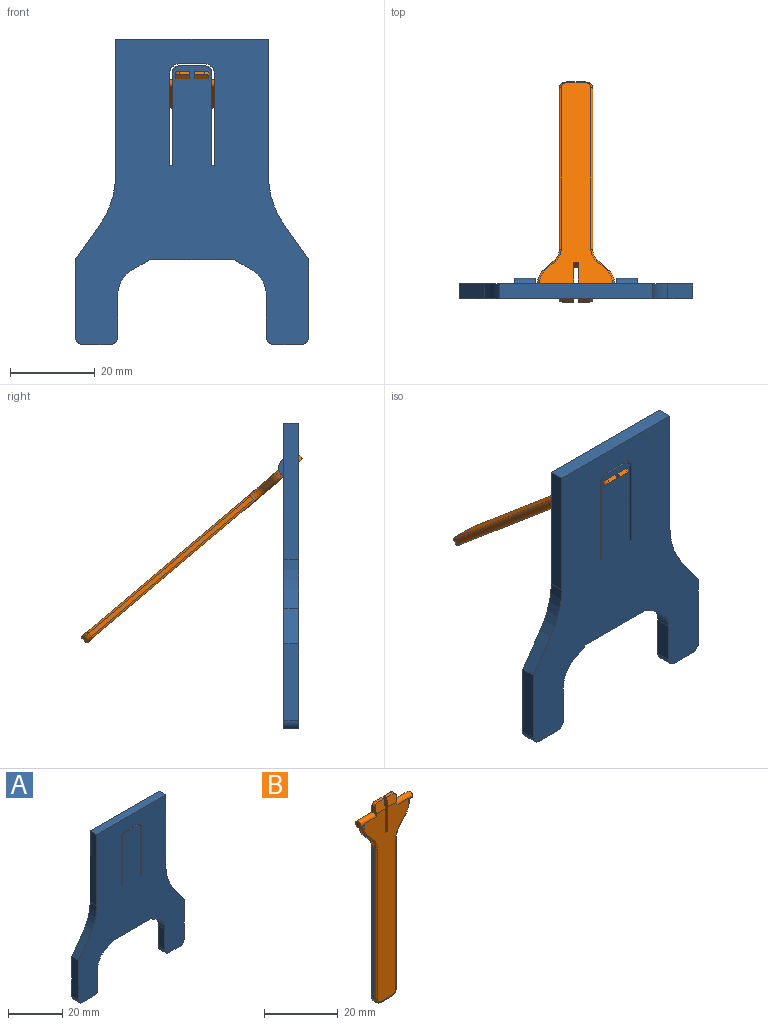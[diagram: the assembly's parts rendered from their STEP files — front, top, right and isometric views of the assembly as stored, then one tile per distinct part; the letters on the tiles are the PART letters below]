
ASSEMBLY  parts=2 mates=1
PART A: 114 faces, bbox 55x4.8x72 mm
  f0: plane 21.71x1.7mm, normal (1,0,0), area 20.6mm2, adj f4,f6,f42,f102,f103,f106,f107,f108
  f1: plane 6x1.6mm, normal (0,0,1), area 9.6mm2, adj f3,f42,f103,f104
  f2: plane 21.71x1.7mm, normal (-1,0,0), area 20.6mm2, adj f4,f6,f42,f104,f105,f106,f107,f108
  f3: cylinder r=0.5mm len=8.88mm, axis (1,0,0), area 7.4mm2, adj f1,f5,f103,f104
  f4: cylinder r=0.5mm len=9.4mm, axis (1,0,0), area 8.7mm2, adj f0,f2,f5,f103,f104,f113
  f5: cylinder r=0.26mm len=9.26mm, axis (1,0,0), area 4.4mm2, adj f3,f4,f103,f104
  f6: plane 39.63x10.4mm, normal (0,1,0), area 394.8mm2, adj f0,f2,f23,f43,f48,f102,f105,f106
  f7: cylinder r=2.2mm len=3.5mm, axis (0,1,0), area 12.1mm2, adj f10,f42,f43,f46
  f8: plane 13.2x5mm, normal (0,1,0), area 42mm2, adj f12,f13,f14,f15,f48,f49,f50,f97
  f9: plane 72x55mm, normal (0,1,0), area 665.1mm2, adj f15,f16,f20,f21,f22,f23,f24,f25
  f10: plane 29x5mm, normal (0,1,0), area 59.9mm2, adj f7,f12,f19,f43,f46,f47,f48,f51
  f11: plane 13.2x5mm, normal (0,1,0), area 42mm2, adj f16,f17,f18,f19,f43,f44,f45,f92
  f12: plane 5x2.7mm, normal (0,0,-1), area 11.8mm2, adj f8,f10,f14,f48,f97,f99
  f13: plane 0.67x0.53mm, normal (-1,0,0), area 0.2mm2, adj f8,f15,f98
  f14: plane 0.23x0.23mm, normal (-1,0,0), area 0mm2, adj f8,f12,f99
  f15: cylinder r=6.2mm len=4.06mm, axis (0,1,0), area 11.6mm2, adj f8,f9,f13,f49,f98
  f16: cylinder r=6.2mm len=4.06mm, axis (0,1,0), area 11.6mm2, adj f9,f11,f17,f45,f93
  f17: plane 0.67x0.53mm, normal (1,0,0), area 0.2mm2, adj f11,f16,f93
  f18: plane 0.23x0.23mm, normal (1,0,0), area 0mm2, adj f11,f19,f94
  f19: plane 5x2.7mm, normal (0,0,-1), area 11.8mm2, adj f10,f11,f18,f43,f92,f94
  f20: plane 9.63x3.5mm, normal (1,0,0), area 33.7mm2, adj f9,f21,f41,f42
  f21: cylinder r=7mm len=6.06mm, axis (0,1,0), area 25.7mm2, adj f9,f20,f22,f42
  f22: plane 4x3.5mm, normal (0.5,0,-0.87), area 16.2mm2, adj f9,f21,f23,f42
  f23: plane 20x3.5mm, normal (0,0,-1), area 41.9mm2, adj f6,f9,f22,f24,f42,f43,f48
  f24: plane 4x3.5mm, normal (-0.5,0,-0.87), area 16.2mm2, adj f9,f23,f25,f42
  f25: cylinder r=7mm len=6.06mm, axis (0,1,0), area 25.7mm2, adj f9,f24,f26,f42
  f26: plane 9.63x3.5mm, normal (-1,0,0), area 33.7mm2, adj f9,f25,f27,f42
  f27: cylinder r=2mm len=3.5mm, axis (0,1,0), area 11mm2, adj f9,f26,f28,f42
  f28: plane 6x3.5mm, normal (0,0,-1), area 21mm2, adj f9,f27,f29,f42
  f29: cylinder r=2mm len=3.5mm, axis (0,1,0), area 11mm2, adj f9,f28,f30,f42
  f30: plane 18x3.5mm, normal (1,0,0), area 63mm2, adj f9,f29,f31,f42
  f31: plane 8.4x5.88mm, normal (0.82,0,0.57), area 35.9mm2, adj f9,f30,f32,f42
  f32: cylinder r=20mm len=11.47mm, axis (0,1,0), area 42.8mm2, adj f9,f31,f33,f42
  f33: plane 32.13x3.5mm, normal (1,0,0), area 112.4mm2, adj f9,f32,f34,f42
  f34: plane 36x3.5mm, normal (0,0,1), area 126mm2, adj f9,f33,f35,f42
  f35: plane 32.13x3.5mm, normal (-1,0,0), area 112.4mm2, adj f9,f34,f36,f42
  f36: cylinder r=20mm len=11.47mm, axis (0,1,0), area 42.8mm2, adj f9,f35,f37,f42
  f37: plane 8.4x5.88mm, normal (-0.82,0,0.57), area 35.9mm2, adj f9,f36,f38,f42
  f38: plane 18x3.5mm, normal (-1,0,0), area 63mm2, adj f9,f37,f39,f42
  f39: cylinder r=2mm len=3.5mm, axis (0,1,0), area 11mm2, adj f9,f38,f40,f42
  f40: plane 6x3.5mm, normal (0,0,-1), area 21mm2, adj f9,f39,f41,f42
  f41: cylinder r=2mm len=3.5mm, axis (0,1,0), area 11mm2, adj f9,f20,f40,f42
  f42: plane 72x55mm, normal (0,-1,0), area 2415.3mm2, adj f0,f1,f2,f7,f20,f21,f22,f23
  f43: plane 44x3.5mm, normal (1,0,0), area 100.5mm2, adj f6,f7,f9,f10,f11,f19,f23,f42
  f44: cylinder r=3.8mm len=2.7mm, axis (0,1,0), area 7.3mm2, adj f9,f11,f43,f45
  f45: plane 2.95x2.7mm, normal (0.76,0,0.65), area 10.5mm2, adj f9,f11,f16,f44
  f46: plane 6x3.5mm, normal (0,0,-1), area 21mm2, adj f7,f10,f42,f47
  f47: cylinder r=2.2mm len=3.5mm, axis (0,1,0), area 12.1mm2, adj f10,f42,f46,f48
  f48: plane 44x3.5mm, normal (-1,0,0), area 100.5mm2, adj f6,f8,f9,f10,f12,f23,f42,f47
  f49: plane 2.95x2.7mm, normal (-0.76,0,0.65), area 10.5mm2, adj f8,f9,f15,f50
  f50: cylinder r=3.8mm len=2.7mm, axis (0,1,0), area 7.3mm2, adj f8,f9,f48,f49
  f51: plane 7x2.75mm, normal (1,0,0), area 14mm2, adj f9,f10,f54,f55,f78,f98
  f52: plane 7x2.75mm, normal (-1,0,0), area 14mm2, adj f9,f10,f56,f78,f91,f93
  f53: plane 1.5x0.35mm, normal (-1,0,0), area 0.4mm2, adj f10,f58,f78,f91
  f54: cylinder r=3.5mm len=2.43mm, axis (1,0,0), area 3.7mm2, adj f9,f51,f78,f87
  f55: cylinder r=3.5mm len=2.3mm, axis (1,0,0), area 3.5mm2, adj f10,f51,f78,f86
  f56: cylinder r=3.5mm len=2.43mm, axis (1,0,0), area 3.7mm2, adj f9,f52,f78,f82
  f57: cylinder r=4.2mm len=4.03mm, axis (0,1,0), area 8.1mm2, adj f10,f78,f84,f85
  f58: plane 5.18x1.5mm, normal (0,0,1), area 7.8mm2, adj f10,f53,f78,f83
  f59: plane 3.34x1.5mm, normal (0,0,1), area 5mm2, adj f9,f64,f78,f90
  f60: plane 9.63x1.5mm, normal (-1,0,0), area 14.4mm2, adj f9,f61,f77,f78
  f61: cylinder r=9mm len=7.79mm, axis (0,1,0), area 14.1mm2, adj f9,f60,f62,f78
  f62: plane 4.46x2.58mm, normal (-0.5,0,0.87), area 7.7mm2, adj f9,f61,f63,f78
  f63: plane 3.34x1.5mm, normal (0,0,1), area 5mm2, adj f9,f62,f78,f79
  f64: plane 4.46x2.58mm, normal (0.5,0,0.87), area 7.7mm2, adj f9,f59,f65,f78
  f65: cylinder r=9mm len=7.79mm, axis (0,1,0), area 14.1mm2, adj f9,f64,f66,f78
  f66: plane 9.63x1.5mm, normal (1,0,0), area 14.4mm2, adj f9,f65,f67,f78
  f67: plane 6x1.5mm, normal (0,0,1), area 9mm2, adj f9,f66,f68,f78
  f68: plane 17.37x1.5mm, normal (-1,0,0), area 26.1mm2, adj f9,f67,f69,f78
  f69: plane 7.89x5.52mm, normal (-0.82,0,-0.57), area 14.4mm2, adj f9,f68,f70,f78
  f70: cylinder r=22mm len=12.62mm, axis (0,1,0), area 20.2mm2, adj f9,f69,f71,f78
  f71: plane 30.13x1.5mm, normal (-1,0,0), area 45.2mm2, adj f9,f70,f72,f78
  f72: plane 32x1.5mm, normal (0,0,-1), area 48mm2, adj f9,f71,f73,f78
  f73: plane 30.13x1.5mm, normal (1,0,0), area 45.2mm2, adj f9,f72,f74,f78
  f74: cylinder r=22mm len=12.62mm, axis (0,1,0), area 20.2mm2, adj f9,f73,f75,f78
  f75: plane 7.89x5.52mm, normal (0.82,0,-0.57), area 14.4mm2, adj f9,f74,f76,f78
  f76: plane 17.37x1.5mm, normal (1,0,0), area 26.1mm2, adj f9,f75,f77,f78
  f77: plane 6x1.5mm, normal (0,0,1), area 9mm2, adj f9,f60,f76,f78
  f78: plane 68x51mm, normal (0,1,0), area 1115.3mm2, adj f51,f52,f53,f54,f55,f56,f57,f58
  f79: plane 28x1.5mm, normal (-1,0,0), area 42mm2, adj f9,f63,f78,f80
  f80: cylinder r=1.8mm len=1.5mm, axis (0,1,0), area 1.9mm2, adj f9,f78,f79,f81
  f81: plane 2.95x2.56mm, normal (-0.76,0,-0.65), area 5.9mm2, adj f9,f78,f80,f82
  f82: cylinder r=8.2mm len=4.02mm, axis (0,1,0), area 6.6mm2, adj f9,f56,f78,f81
  f83: cylinder r=4.2mm len=4.03mm, axis (0,1,0), area 8.1mm2, adj f10,f58,f78,f84
  f84: plane 6x1.5mm, normal (0,0,1), area 9mm2, adj f10,f57,f78,f83
  f85: plane 5.18x1.5mm, normal (0,0,1), area 7.8mm2, adj f10,f57,f78,f86
  f86: plane 1.5x0.35mm, normal (1,0,0), area 0.4mm2, adj f10,f55,f78,f85
  f87: cylinder r=8.2mm len=4.02mm, axis (0,1,0), area 6.6mm2, adj f9,f54,f78,f88
  f88: plane 2.95x2.56mm, normal (0.76,0,-0.65), area 5.9mm2, adj f9,f78,f87,f89
  f89: cylinder r=1.8mm len=1.5mm, axis (0,1,0), area 1.9mm2, adj f9,f78,f88,f90
  f90: plane 28x1.5mm, normal (1,0,0), area 42mm2, adj f9,f59,f78,f89
  f91: cylinder r=3.5mm len=2.3mm, axis (1,0,0), area 3.5mm2, adj f10,f52,f53,f78
  f92: plane 4.27x3.95mm, normal (1,0,0), area 6.7mm2, adj f10,f11,f19,f93,f94,f95
  f93: cylinder r=2.25mm len=5mm, axis (-1,0,0), area 27.1mm2, adj f9,f10,f11,f16,f17,f52,f92
  f94: cylinder r=2.25mm len=0.7mm, axis (-1,0,0), area 0.2mm2, adj f11,f18,f19,f92
  f95: cylinder r=1.5mm len=3mm, axis (1,0,0), area 28.3mm2, adj f92,f96
  f96: plane 3x3mm, normal (1,0,0), area 7.1mm2, adj f95
  f97: plane 4.27x3.95mm, normal (-1,0,0), area 6.7mm2, adj f8,f10,f12,f98,f99,f100
  f98: cylinder r=2.25mm len=5mm, axis (-1,0,0), area 27.1mm2, adj f8,f9,f10,f13,f15,f51,f97
  f99: cylinder r=2.25mm len=0.7mm, axis (-1,0,0), area 0.2mm2, adj f8,f12,f14,f97
  f100: cylinder r=1.5mm len=3mm, axis (1,0,0), area 28.3mm2, adj f97,f101
  f101: plane 3x3mm, normal (-1,0,0), area 7.1mm2, adj f100
  f102: plane 0.8x0.5mm, normal (0,0,1), area 0.4mm2, adj f0,f6,f42,f48
  f103: cylinder r=1.7mm len=1.7mm, axis (0,1,0), area 4mm2, adj f0,f1,f3,f4,f5,f42
  f104: cylinder r=1.7mm len=1.7mm, axis (0,1,0), area 4mm2, adj f1,f2,f3,f4,f5,f42
  f105: plane 0.8x0.5mm, normal (0,0,1), area 0.4mm2, adj f2,f6,f42,f43
  f106: plane 9.4x0.8mm, normal (0,0,-1), area 7.5mm2, adj f0,f2,f6,f107
  f107: cylinder r=0.26mm len=9.4mm, axis (1,0,0), area 4.5mm2, adj f0,f2,f106,f108
  f108: cylinder r=0.5mm len=9.4mm, axis (1,0,0), area 8.7mm2, adj f0,f2,f107,f109
  f109: cylinder r=0.26mm len=9.4mm, axis (1,0,0), area 4.5mm2, adj f0,f2,f108,f110
  f110: cylinder r=0.5mm len=9.4mm, axis (1,0,0), area 8.7mm2, adj f0,f2,f109,f111
  f111: cylinder r=0.26mm len=9.4mm, axis (1,0,0), area 4.5mm2, adj f0,f2,f110,f112
  f112: cylinder r=0.5mm len=9.4mm, axis (1,0,0), area 8.7mm2, adj f0,f2,f111,f113
  f113: cylinder r=0.26mm len=9.4mm, axis (1,0,0), area 4.5mm2, adj f0,f2,f4,f112
PART B: 58 faces, bbox 20x2x67.2 mm
  f0: plane 63.5x17mm, normal (0,-1,0), area 497.5mm2, adj f6,f9,f10,f14,f16,f25,f26,f27
  f1: plane 63.5x17mm, normal (0,1,0), area 497.5mm2, adj f6,f9,f10,f14,f17,f18,f19,f20
  f2: cylinder r=5mm len=3.27mm, axis (0,1,0), area 3.6mm2, adj f3,f13,f21,f28
  f3: plane 2.95x2.56mm, normal (0.76,0,-0.65), area 3.9mm2, adj f2,f4,f20,f27
  f4: cylinder r=5mm len=3.27mm, axis (0,1,0), area 3.6mm2, adj f3,f5,f19,f26
  f5: plane 1x0.63mm, normal (1,0,0), area 0.5mm2, adj f4,f14,f18,f25
  f6: plane 3x2mm, normal (1,0,0), area 3.8mm2, adj f0,f1,f7,f14,f16,f17
  f7: cylinder r=1mm len=1.33mm, axis (0,1,0), area 1.8mm2, adj f6,f8,f16,f17
  f8: plane 2.5x1mm, normal (0,0,1), area 2.5mm2, adj f7,f9,f16,f17
  f9: plane 11x2mm, normal (-1,0,0), area 20.5mm2, adj f0,f1,f8,f10,f16,f17
  f10: plane 2x1mm, normal (0,0,1), area 2mm2, adj f0,f1,f9,f39
  f11: plane 4x1mm, normal (0,0,-1), area 4mm2, adj f12,f24,f31,f40
  f12: cylinder r=2mm len=2mm, axis (0,1,0), area 3.1mm2, adj f11,f13,f23,f30
  f13: plane 50x1mm, normal (1,0,0), area 50mm2, adj f2,f12,f22,f29
  f14: cylinder r=1mm len=6mm, axis (1,0,0), area 22.4mm2, adj f0,f1,f5,f6,f15,f18,f25
  f15: plane 2x2mm, normal (1,0,0), area 3.1mm2, adj f14
  f16: plane 3.5x3mm, normal (0,-0.99,0.16), area 10.4mm2, adj f0,f6,f7,f8,f9
  f17: plane 3.5x3mm, normal (0,0.99,0.16), area 10.4mm2, adj f1,f6,f7,f8,f9
  f18: cylinder r=0.5mm len=1.5mm, axis (0,0,1), area 0.8mm2, adj f1,f5,f14,f19
  f19: torus R=4.5mm, axis (0,-1,0), area 2.7mm2, adj f1,f4,f18,f20
  f20: cylinder r=0.5mm len=3.28mm, axis (0.65,0,0.76), area 3.1mm2, adj f1,f3,f19,f21
  f21: torus R=5.5mm, axis (0,-1,0), area 2.9mm2, adj f1,f2,f20,f22
  f22: cylinder r=0.5mm len=50mm, axis (0,0,1), area 39.3mm2, adj f1,f13,f21,f23
  f23: torus R=1.5mm, axis (0,-1,0), area 2.2mm2, adj f1,f12,f22,f24
  f24: cylinder r=0.5mm len=4mm, axis (1,0,0), area 3.1mm2, adj f1,f11,f23,f51
  f25: cylinder r=0.5mm len=1.5mm, axis (0,0,-1), area 0.8mm2, adj f0,f5,f14,f26
  f26: torus R=4.5mm, axis (0,-1,0), area 2.7mm2, adj f0,f4,f25,f27
  f27: cylinder r=0.5mm len=3.28mm, axis (-0.65,0,-0.76), area 3.1mm2, adj f0,f3,f26,f28
  f28: torus R=5.5mm, axis (0,-1,0), area 2.9mm2, adj f0,f2,f27,f29
  f29: cylinder r=0.5mm len=50mm, axis (0,0,-1), area 39.3mm2, adj f0,f13,f28,f30
  f30: torus R=1.5mm, axis (0,-1,0), area 2.2mm2, adj f0,f12,f29,f31
  f31: cylinder r=0.5mm len=4mm, axis (-1,0,0), area 3.1mm2, adj f0,f11,f30,f57
  f32: cylinder r=5mm len=3.27mm, axis (0,1,0), area 3.6mm2, adj f33,f41,f49,f55
  f33: plane 2.95x2.56mm, normal (-0.76,0,-0.65), area 3.9mm2, adj f32,f34,f48,f54
  f34: cylinder r=5mm len=3.27mm, axis (0,1,0), area 3.6mm2, adj f33,f35,f47,f53
  f35: plane 1x0.63mm, normal (-1,0,0), area 0.5mm2, adj f34,f42,f46,f52
  f36: plane 3x2mm, normal (-1,0,0), area 3.8mm2, adj f0,f1,f37,f42,f44,f45
  f37: cylinder r=1mm len=1.33mm, axis (0,1,0), area 1.8mm2, adj f36,f38,f44,f45
  f38: plane 2.5x1mm, normal (0,0,1), area 2.5mm2, adj f37,f39,f44,f45
  f39: plane 11x2mm, normal (1,0,0), area 20.5mm2, adj f0,f1,f10,f38,f44,f45
  f40: cylinder r=2mm len=2mm, axis (0,1,0), area 3.1mm2, adj f11,f41,f51,f57
  f41: plane 50x1mm, normal (-1,0,0), area 50mm2, adj f32,f40,f50,f56
  f42: cylinder r=1mm len=6mm, axis (-1,0,0), area 22.4mm2, adj f0,f1,f35,f36,f43,f46,f52
  f43: plane 2x2mm, normal (-1,0,0), area 3.1mm2, adj f42
  f44: plane 3.5x3mm, normal (0,-0.99,0.16), area 10.4mm2, adj f0,f36,f37,f38,f39
  f45: plane 3.5x3mm, normal (0,0.99,0.16), area 10.4mm2, adj f1,f36,f37,f38,f39
  f46: cylinder r=0.5mm len=1.5mm, axis (0,0,1), area 0.8mm2, adj f1,f35,f42,f47
  f47: torus R=4.5mm, axis (0,-1,0), area 2.7mm2, adj f1,f34,f46,f48
  f48: cylinder r=0.5mm len=3.28mm, axis (-0.65,0,0.76), area 3.1mm2, adj f1,f33,f47,f49
  f49: torus R=5.5mm, axis (0,-1,0), area 2.9mm2, adj f1,f32,f48,f50
  f50: cylinder r=0.5mm len=50mm, axis (0,0,1), area 39.3mm2, adj f1,f41,f49,f51
  f51: torus R=1.5mm, axis (0,-1,0), area 2.2mm2, adj f1,f24,f40,f50
  f52: cylinder r=0.5mm len=1.5mm, axis (0,0,-1), area 0.8mm2, adj f0,f35,f42,f53
  f53: torus R=4.5mm, axis (0,-1,0), area 2.7mm2, adj f0,f34,f52,f54
  f54: cylinder r=0.5mm len=3.28mm, axis (0.65,0,-0.76), area 3.1mm2, adj f0,f33,f53,f55
  f55: torus R=5.5mm, axis (0,-1,0), area 2.9mm2, adj f0,f32,f54,f56
  f56: cylinder r=0.5mm len=50mm, axis (0,0,-1), area 39.3mm2, adj f0,f41,f55,f57
  f57: torus R=1.5mm, axis (0,-1,0), area 2.2mm2, adj f0,f31,f40,f56
PLACE A t=(0,3.5,23.63)mm
PLACE B rot(axis=(1,0,0),49.8deg) t=(0,2.38,24.54)mm
MATE revolute A.f54 <-> B.f14  axis (-1,0,0) through (9.5,2.5,23.13)mm
